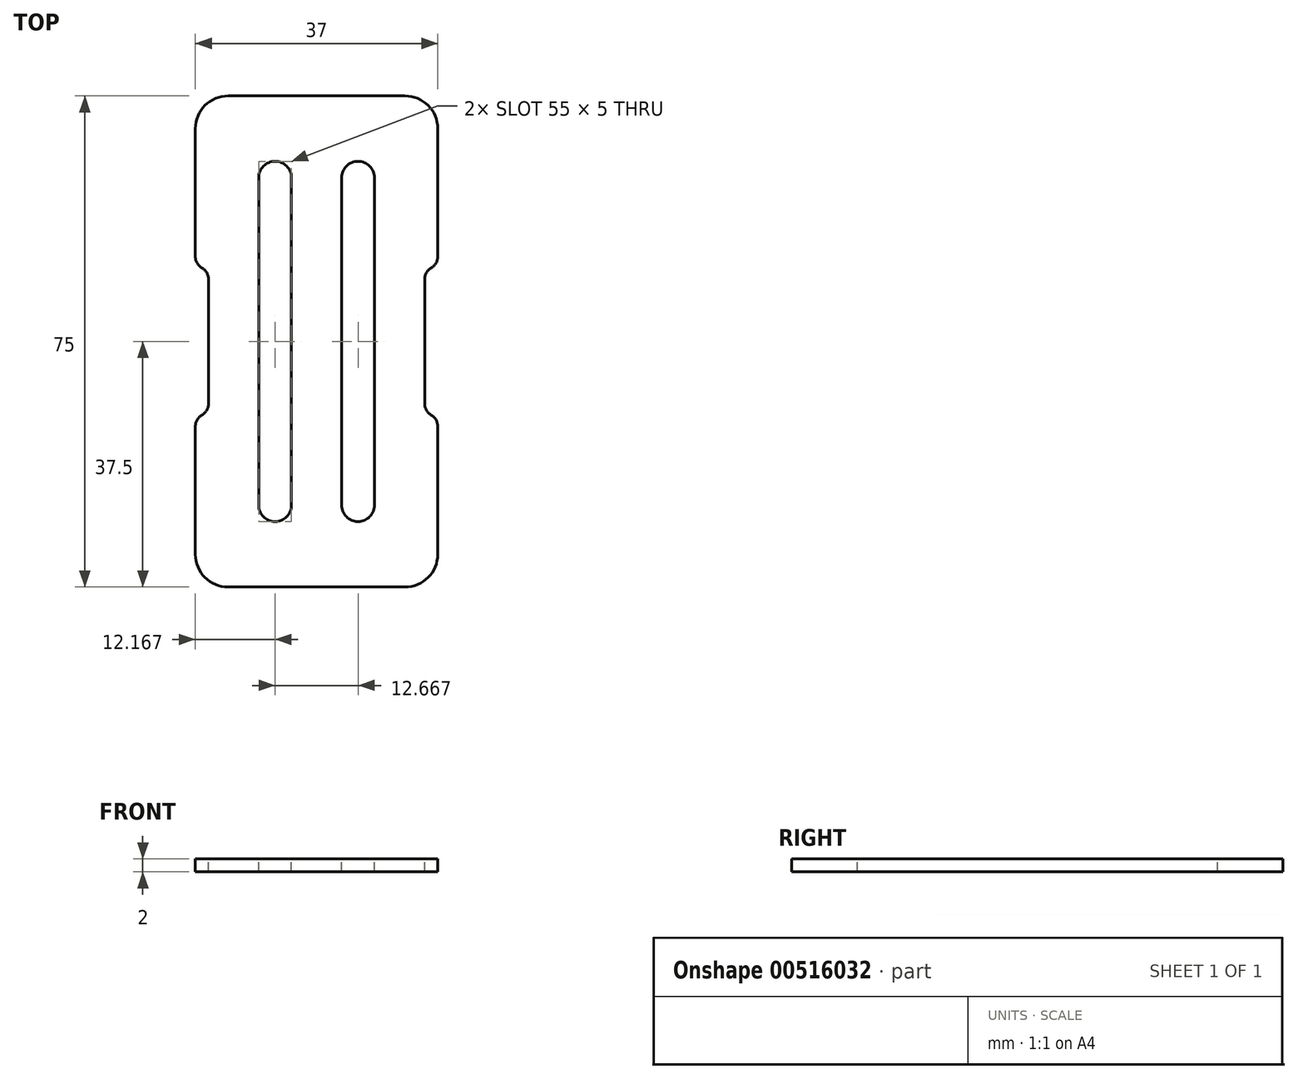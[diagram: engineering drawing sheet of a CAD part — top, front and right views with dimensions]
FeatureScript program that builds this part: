
annotation { "Feature Type Name" : "Feature", "Feature Type Description" : "" }
export const myFeature = defineFeature(function(context is Context, id is Id, definition is map)
    precondition{}
    {
        {
            var Q0;
            Q0=qCreatedBy(makeId("Top.planeOp"),FACE);
            var sketch = newSketch(context, id + "F0", { "sketchPlane" : qUnion([Q0])});
            skLineSegment(sketch, "E0.bottom", {"start": v(-18.5, -37.5) * mm, "end": v(18.5, -37.5) * mm});
            skLineSegment(sketch, "E0.top", {"start": v(-18.5, 37.5) * mm, "end": v(18.5, 37.5) * mm});
            skLineSegment(sketch, "E0.left", {"start": v(-18.5, -37.5) * mm, "end": v(-18.5, 37.5) * mm});
            skLineSegment(sketch, "E0.right", {"start": v(18.5, -37.5) * mm, "end": v(18.5, 37.5) * mm});
            skSolve(sketch);
        }
        {
            var Q0;
            Q0=qSketchRegion(id+"F0",true);
            extrude(context, id + "F1", {"entities" : qUnion([Q0]), "depth" : 2 * mm, "offsetDistance" : 25 * mm});
        }
        {
            var Q0;
            Q0=makeQuery(id+"F1.opExtrude","SWEPT_EDGE",EDGE,{"disambiguationData":[OSD([sQuery(id+"F0.wireOp",EDGE,"E0.bottom"),sQuery(id+"F0.wireOp",EDGE,"E0.right")])]});
            var Q1;
            Q1=makeQuery(id+"F1.opExtrude","SWEPT_EDGE",EDGE,{"disambiguationData":[OSD([sQuery(id+"F0.wireOp",EDGE,"E0.bottom"),sQuery(id+"F0.wireOp",EDGE,"E0.left")])]});
            var Q2;
            Q2=makeQuery(id+"F1.opExtrude","SWEPT_EDGE",EDGE,{"disambiguationData":[OSD([sQuery(id+"F0.wireOp",EDGE,"E0.top"),sQuery(id+"F0.wireOp",EDGE,"E0.right")])]});
            var Q3;
            Q3=makeQuery(id+"F1.opExtrude","SWEPT_EDGE",EDGE,{"disambiguationData":[OSD([sQuery(id+"F0.wireOp",EDGE,"E0.top"),sQuery(id+"F0.wireOp",EDGE,"E0.left")])]});
            fillet(context, id + "F2", {"entities" : qUnion([Q0, Q1, Q2, Q3]), "radius" : 5 * mm, "tangentPropagation" : true, "allowEdgeOverflow" : false});
        }
        {
            var Q0;
            Q0=makeQuery(id+"F1.opExtrude","CAP_FACE",FACE,{"disambiguationData":[OSD([sQuery(id+"F0.wireOp",EDGE,"E0.bottom"),sQuery(id+"F0.wireOp",EDGE,"E0.top"),sQuery(id+"F0.wireOp",EDGE,"E0.left"),sQuery(id+"F0.wireOp",EDGE,"E0.right")])],"isStart":false});
            var sketch = newSketch(context, id + "F3", { "sketchPlane" : qUnion([Q0])});
            skLineSegment(sketch, "E1.bottom", {"start": v(-18.5, -11.5) * mm, "end": v(-16.5, -11.5) * mm});
            skLineSegment(sketch, "E1.top", {"start": v(-18.5, 11.5) * mm, "end": v(-16.5, 11.5) * mm});
            skLineSegment(sketch, "E1.left", {"start": v(-18.5, -11.5) * mm, "end": v(-18.5, 11.5) * mm});
            skLineSegment(sketch, "E1.right", {"start": v(-16.5, -11.5) * mm, "end": v(-16.5, 11.5) * mm});
            skLineSegment(sketch, "E2.bottom", {"start": v(18.5, 11.5) * mm, "end": v(16.5, 11.5) * mm});
            skLineSegment(sketch, "E2.top", {"start": v(18.5, -11.5) * mm, "end": v(16.5, -11.5) * mm});
            skLineSegment(sketch, "E2.left", {"start": v(18.5, 11.5) * mm, "end": v(18.5, -11.5) * mm});
            skLineSegment(sketch, "E2.right", {"start": v(16.5, 11.5) * mm, "end": v(16.5, -11.5) * mm});
            skSolve(sketch);
        }
        {
            var Q0;
            Q0 = qSketchRegion(id + "F3", true);
            extrude(context, id + "F4", {"entities" : qUnion([Q0]), "operationType" : NewBodyOperationType.REMOVE, "endBound" : BoundingType.THROUGH_ALL, "oppositeDirection" : true, "depth" : 25 * mm, "offsetDistance" : 25 * mm});
        }
        {
            var Q0;
            Q0=makeQuery(id+"F4.boolean.opBoolean","COPY",EDGE,{"derivedFrom":makeQuery(id+"F4.opExtrude","SWEPT_EDGE",EDGE,{"disambiguationData":[OSD([sQuery(id+"F3.wireOp",EDGE,"E1.bottom"),sQuery(id+"F3.wireOp",EDGE,"E1.right")])]})});
            var Q1;
            Q1=makeQuery(id+"F4.boolean.opBoolean","COPY",EDGE,{"derivedFrom":makeQuery(id+"F4.opExtrude","SWEPT_EDGE",EDGE,{"disambiguationData":[OSD([sQuery(id+"F3.wireOp",EDGE,"E1.top"),sQuery(id+"F3.wireOp",EDGE,"E1.right")])]})});
            var Q2;
            Q2=makeQuery(id+"F4.boolean.opBoolean","COPY",EDGE,{"derivedFrom":makeQuery(id+"F4.opExtrude","SWEPT_EDGE",EDGE,{"disambiguationData":[OSD([sQuery(id+"F3.wireOp",EDGE,"E2.bottom"),sQuery(id+"F3.wireOp",EDGE,"E2.right")])]})});
            var Q3;
            Q3=makeQuery(id+"F4.boolean.opBoolean","COPY",EDGE,{"derivedFrom":makeQuery(id+"F4.opExtrude","SWEPT_EDGE",EDGE,{"disambiguationData":[OSD([sQuery(id+"F3.wireOp",EDGE,"E2.top"),sQuery(id+"F3.wireOp",EDGE,"E2.right")])]})});
            fillet(context, id + "F5", {"entities" : qUnion([Q0, Q1, Q2, Q3]), "radius" : 2 * mm, "tangentPropagation" : true, "allowEdgeOverflow" : false});
        }
        {
            var Q0;
            {var subQ0=sQuery(id+"F0.wireOp",EDGE,"E0.right");var subQ4=sQuery(id+"F3.wireOp",EDGE,"E2.top");Q0=makeQuery(id+"F5.opFillet","BLEND_EDGE",EDGE,{"blendedFrom":[makeQuery(id+"F4.boolean.opBoolean","COPY",EDGE,{"derivedFrom":makeQuery(id+"F4.opExtrude","SWEPT_EDGE",EDGE,{"disambiguationData":[OSD([subQ4,sQuery(id+"F3.wireOp",EDGE,"E2.right")])]})}),makeQuery(id+"F4.boolean.opBoolean","SPLIT",FACE,{"disambiguationData":[TD([makeQuery(id+"F4.opExtrude","SWEPT_FACE",FACE,{"disambiguationData":[OSD([subQ4])]})])],"derivedFrom":makeQuery(id+"F1.opExtrude","SWEPT_FACE",FACE,{"disambiguationData":[OSD([subQ0])]})})],"blendedInto":[makeQuery(id+"F4.boolean.opBoolean","SPLIT",FACE,{"disambiguationData":[TD([makeQuery(id+"F4.opExtrude","SWEPT_FACE",FACE,{"disambiguationData":[OSD([subQ4])]})])],"derivedFrom":makeQuery(id+"F1.opExtrude","SWEPT_FACE",FACE,{"disambiguationData":[OSD([subQ0])]})})]});}
            var Q1;
            {var subQ0=sQuery(id+"F0.wireOp",EDGE,"E0.right");var subQ4=sQuery(id+"F3.wireOp",EDGE,"E2.bottom");Q1=makeQuery(id+"F5.opFillet","BLEND_EDGE",EDGE,{"blendedFrom":[makeQuery(id+"F4.boolean.opBoolean","COPY",EDGE,{"derivedFrom":makeQuery(id+"F4.opExtrude","SWEPT_EDGE",EDGE,{"disambiguationData":[OSD([subQ4,sQuery(id+"F3.wireOp",EDGE,"E2.right")])]})}),makeQuery(id+"F4.boolean.opBoolean","SPLIT",FACE,{"disambiguationData":[TD([makeQuery(id+"F4.opExtrude","SWEPT_FACE",FACE,{"disambiguationData":[OSD([subQ4])]})])],"derivedFrom":makeQuery(id+"F1.opExtrude","SWEPT_FACE",FACE,{"disambiguationData":[OSD([subQ0])]})})],"blendedInto":[makeQuery(id+"F4.boolean.opBoolean","SPLIT",FACE,{"disambiguationData":[TD([makeQuery(id+"F4.opExtrude","SWEPT_FACE",FACE,{"disambiguationData":[OSD([subQ4])]})])],"derivedFrom":makeQuery(id+"F1.opExtrude","SWEPT_FACE",FACE,{"disambiguationData":[OSD([subQ0])]})})]});}
            var Q2;
            {var subQ1=sQuery(id+"F0.wireOp",EDGE,"E0.left");var subQ4=sQuery(id+"F3.wireOp",EDGE,"E1.top");Q2=makeQuery(id+"F5.opFillet","BLEND_EDGE",EDGE,{"blendedFrom":[makeQuery(id+"F4.boolean.opBoolean","COPY",EDGE,{"derivedFrom":makeQuery(id+"F4.opExtrude","SWEPT_EDGE",EDGE,{"disambiguationData":[OSD([subQ4,sQuery(id+"F3.wireOp",EDGE,"E1.right")])]})}),makeQuery(id+"F4.boolean.opBoolean","SPLIT",FACE,{"disambiguationData":[TD([makeQuery(id+"F4.opExtrude","SWEPT_FACE",FACE,{"disambiguationData":[OSD([subQ4])]})])],"derivedFrom":makeQuery(id+"F1.opExtrude","SWEPT_FACE",FACE,{"disambiguationData":[OSD([subQ1])]})})],"blendedInto":[makeQuery(id+"F4.boolean.opBoolean","SPLIT",FACE,{"disambiguationData":[TD([makeQuery(id+"F4.opExtrude","SWEPT_FACE",FACE,{"disambiguationData":[OSD([subQ4])]})])],"derivedFrom":makeQuery(id+"F1.opExtrude","SWEPT_FACE",FACE,{"disambiguationData":[OSD([subQ1])]})})]});}
            var Q3;
            {var subQ1=sQuery(id+"F0.wireOp",EDGE,"E0.left");var subQ4=sQuery(id+"F3.wireOp",EDGE,"E1.bottom");Q3=makeQuery(id+"F5.opFillet","BLEND_EDGE",EDGE,{"blendedFrom":[makeQuery(id+"F4.boolean.opBoolean","COPY",EDGE,{"derivedFrom":makeQuery(id+"F4.opExtrude","SWEPT_EDGE",EDGE,{"disambiguationData":[OSD([subQ4,sQuery(id+"F3.wireOp",EDGE,"E1.right")])]})}),makeQuery(id+"F4.boolean.opBoolean","SPLIT",FACE,{"disambiguationData":[TD([makeQuery(id+"F4.opExtrude","SWEPT_FACE",FACE,{"disambiguationData":[OSD([subQ4])]})])],"derivedFrom":makeQuery(id+"F1.opExtrude","SWEPT_FACE",FACE,{"disambiguationData":[OSD([subQ1])]})})],"blendedInto":[makeQuery(id+"F4.boolean.opBoolean","SPLIT",FACE,{"disambiguationData":[TD([makeQuery(id+"F4.opExtrude","SWEPT_FACE",FACE,{"disambiguationData":[OSD([subQ4])]})])],"derivedFrom":makeQuery(id+"F1.opExtrude","SWEPT_FACE",FACE,{"disambiguationData":[OSD([subQ1])]})})]});}
            fillet(context, id + "F6", {"entities" : qUnion([Q0, Q1, Q2, Q3]), "radius" : 2 * mm, "tangentPropagation" : true, "allowEdgeOverflow" : false});
        }
        {
            var Q0;
            Q0=makeQuery(id+"F1.opExtrude","CAP_FACE",FACE,{"disambiguationData":[OSD([sQuery(id+"F0.wireOp",EDGE,"E0.bottom"),sQuery(id+"F0.wireOp",EDGE,"E0.top"),sQuery(id+"F0.wireOp",EDGE,"E0.left"),sQuery(id+"F0.wireOp",EDGE,"E0.right")])],"isStart":false});
            var sketch = newSketch(context, id + "F7", { "sketchPlane" : qUnion([Q0])});
            skLineSegment(sketch, "E3.bottom", {"start": v(-8.83, 25) * mm, "end": v(-3.83, 25) * mm, "construction": true});
            skLineSegment(sketch, "E3.top", {"start": v(-8.83, -25) * mm, "end": v(-3.83, -25) * mm, "construction": true});
            skLineSegment(sketch, "E3.left", {"start": v(-8.83, 25) * mm, "end": v(-8.83, -25) * mm});
            skLineSegment(sketch, "E3.right", {"start": v(-3.83, 25) * mm, "end": v(-3.83, -25) * mm});
            skLineSegment(sketch, "E4.bottom", {"start": v(3.83, 25) * mm, "end": v(8.83, 25) * mm, "construction": true});
            skLineSegment(sketch, "E4.top", {"start": v(3.83, -25) * mm, "end": v(8.83, -25) * mm, "construction": true});
            skLineSegment(sketch, "E4.left", {"start": v(3.83, 25) * mm, "end": v(3.83, -25) * mm});
            skLineSegment(sketch, "E4.right", {"start": v(8.83, 25) * mm, "end": v(8.83, -25) * mm});
            skLineSegment(sketch, "E5", {"start": v(-16.5, 0) * mm, "end": v(-8.83, 0) * mm, "construction": true});
            skLineSegment(sketch, "E6", {"start": v(-3.83, 0) * mm, "end": v(3.83, 0) * mm, "construction": true});
            skPoint(sketch, "E6.endSnap0", {"position": v(3.83, 0) * mm});
            skLineSegment(sketch, "E7", {"start": v(8.83, 0) * mm, "end": v(16.5, 0) * mm, "construction": true});
            skArc(sketch, "E8", {"start": v(-3.83, 25) * mm, "mid": v(-6.33, 27.5) * mm, "end": v(-8.83, 25) * mm});
            skArc(sketch, "E9", {"start": v(3.83, 25) * mm, "mid": v(6.33, 27.5) * mm, "end": v(8.83, 25) * mm});
            skArc(sketch, "E10", {"start": v(-8.83, -25) * mm, "mid": v(-6.33, -27.5) * mm, "end": v(-3.83, -25) * mm});
            skArc(sketch, "E11", {"start": v(3.83, -25) * mm, "mid": v(6.33, -27.5) * mm, "end": v(8.83, -25) * mm});
            skSolve(sketch);
        }
        {
            var Q0;
            Q0 = qSketchRegion(id + "F7", true);
            extrude(context, id + "F8", {"entities" : qUnion([Q0]), "operationType" : NewBodyOperationType.REMOVE, "endBound" : BoundingType.THROUGH_ALL, "oppositeDirection" : true, "depth" : 25 * mm, "offsetDistance" : 25 * mm});
        }
    });
